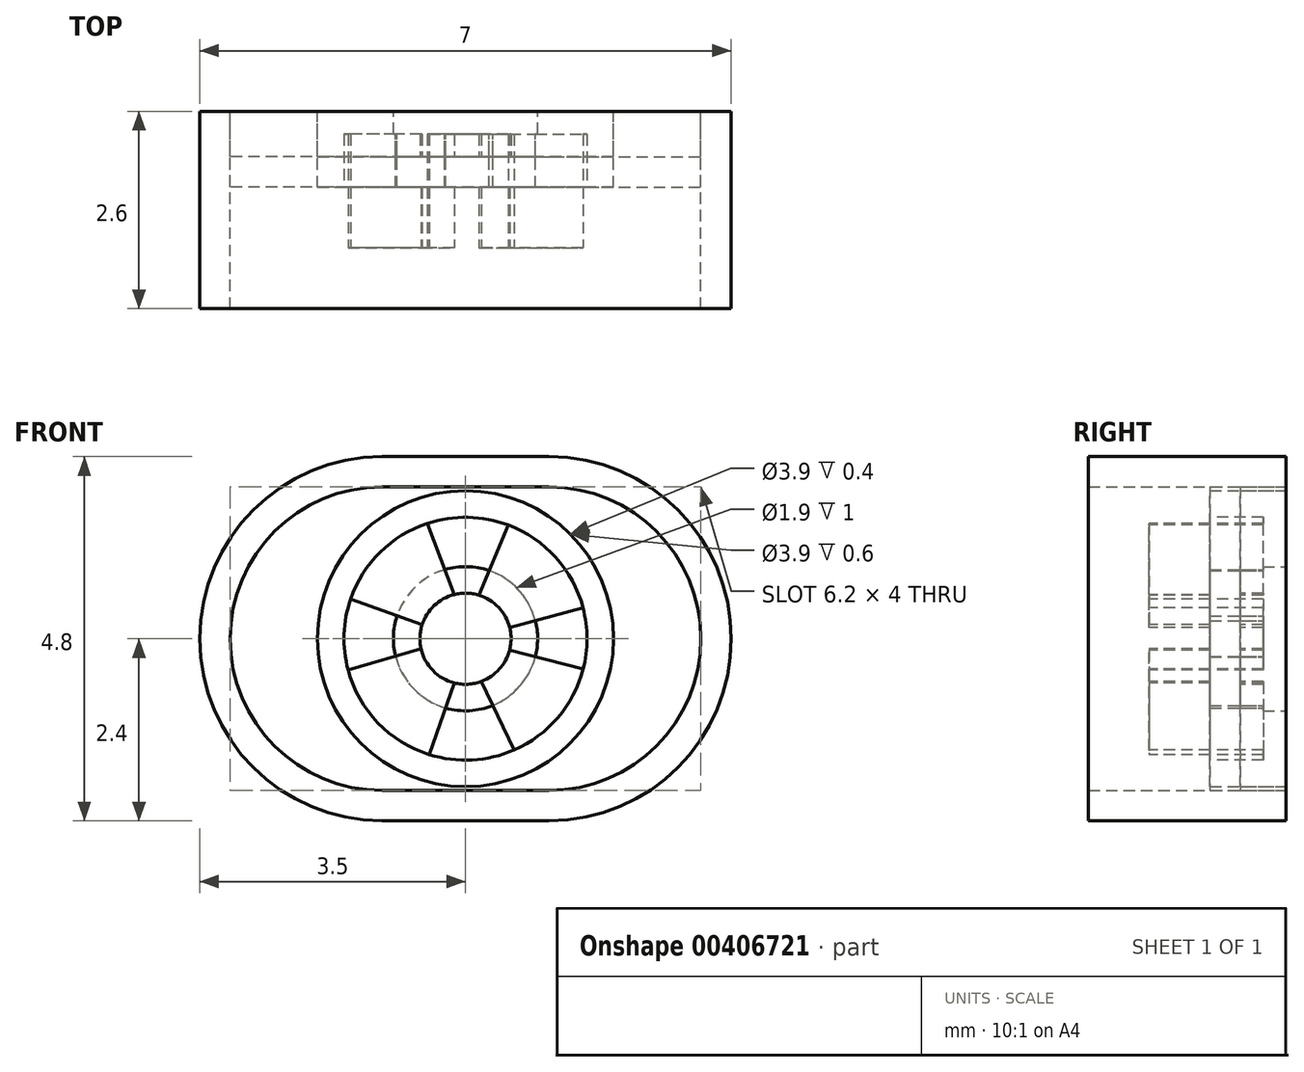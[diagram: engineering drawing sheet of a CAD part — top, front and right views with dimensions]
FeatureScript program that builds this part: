
annotation { "Feature Type Name" : "Feature", "Feature Type Description" : "" }
export const myFeature = defineFeature(function(context is Context, id is Id, definition is map)
    precondition{}
    {
        {
            var Q0;
            Q0=qCreatedBy(makeId("Front.planeOp"),FACE);
            var sketch = newSketch(context, id + "F0", { "sketchPlane" : qUnion([Q0])});
            skLineSegment(sketch, "E0", {"start": v(0, 0) * mm, "end": v(2.2, 0) * mm});
            skLineSegment(sketch, "E1", {"start": v(0, -4.8) * mm, "end": v(2.2, -4.8) * mm});
            skArc(sketch, "E2", {"start": v(0, 0) * mm, "mid": v(-2.4, -2.4) * mm, "end": v(0, -4.8) * mm});
            skArc(sketch, "E3", {"start": v(2.2, -4.8) * mm, "mid": v(4.6, -2.4) * mm, "end": v(2.2, 0) * mm});
            skLineSegment(sketch, "E4.0", {"start": v(0, -4.4) * mm, "end": v(2.2, -4.4) * mm});
            skArc(sketch, "E4.1", {"start": v(0, -0.4) * mm, "mid": v(-2, -2.4) * mm, "end": v(0, -4.4) * mm});
            skLineSegment(sketch, "E4.2", {"start": v(0, -0.4) * mm, "end": v(2.2, -0.4) * mm});
            skArc(sketch, "E4.3", {"start": v(2.2, -4.4) * mm, "mid": v(4.2, -2.4) * mm, "end": v(2.2, -0.4) * mm});
            skCircle(sketch, "E5", {"center": v(1.1, -2.4) * mm, "radius": 0.95 * mm});
            skCircle(sketch, "E6.0", {"center": v(1.1, -2.4) * mm, "radius": 1.95 * mm});
            skSolve(sketch);
        }
        {
            var Q0;
            Q0 = qSketchRegion(id + "F0", true);
            extrude(context, id + "F1", {"entities" : qUnion([Q0]), "depth" : 2.6 * mm});
        }
        {
            var Q0;
            Q0=makeQuery(id+"F0.imprint","IMPRINT",FACE,{"disambiguationData":[TD([[makeQuery(id+"F0.imprint","IMPRINT",EDGE,{"derivedFrom":sQuery(id+"F0.wireOp",EDGE,"E5")}),-1.0]])]});
            extrude(context, id + "F2", {"entities" : qUnion([Q0]), "depth" : 1 * mm});
        }
        {
            var Q0;
            Q0=makeQuery(id+"F0.imprint","IMPRINT",FACE,{"disambiguationData":[TD([[makeQuery(id+"F0.imprint","IMPRINT",EDGE,{"derivedFrom":sQuery(id+"F0.wireOp",EDGE,"E4.0")}),1.0]])]});
            var Q1;
            Q1=makeQuery(id+"F0.imprint","IMPRINT",FACE,{"disambiguationData":[TD([[makeQuery(id+"F0.imprint","IMPRINT",EDGE,{"derivedFrom":sQuery(id+"F0.wireOp",EDGE,"E5")}),1.0]])]});
            extrude(context, id + "F3", {"entities" : qUnion([Q0, Q1]), "depth" : 0.6 * mm});
        }
        {
            var Q0;
            Q0=makeQuery(id+"F2.opExtrude","CAP_FACE",FACE,{"disambiguationData":[OSD([sQuery(id+"F0.wireOp",EDGE,"E5"),sQuery(id+"F0.wireOp",EDGE,"E6.0")])],"isStart":false});
            var sketch = newSketch(context, id + "F4", { "sketchPlane" : qUnion([Q0])});
            skCircle(sketch, "E7", {"center": v(1.1, -2.4) * mm, "radius": 0.6 * mm});
            skCircle(sketch, "E8.0", {"center": v(1.1, -2.4) * mm, "radius": 1.6 * mm});
            skSolve(sketch);
        }
        {
            var Q0;
            Q0=makeQuery(id+"F3.opExtrude","CAP_FACE",FACE,{"disambiguationData":[OSD([sQuery(id+"F0.wireOp",EDGE,"E4.0"),sQuery(id+"F0.wireOp",EDGE,"E4.1"),sQuery(id+"F0.wireOp",EDGE,"E4.2"),sQuery(id+"F0.wireOp",EDGE,"E4.3"),sQuery(id+"F0.wireOp",EDGE,"E6.0")])],"isStart":false});
            extrude(context, id + "F5", {"entities" : qUnion([Q0]), "depth" : 0.4 * mm});
        }
        {
            var Q0;
            Q0=makeQuery(id+"F4.imprint","IMPRINT",FACE,{"disambiguationData":[TD([[makeQuery(id+"F4.imprint","IMPRINT",EDGE,{"derivedFrom":sQuery(id+"F4.wireOp",EDGE,"E7")}),-1.0]])]});
            var Q1;
            Q1=makeQuery(id+"F4.imprint","IMPRINT",FACE,{"disambiguationData":[TD([[makeQuery(id+"F4.imprint","IMPRINT",EDGE,{"derivedFrom":sQuery(id+"F4.wireOp",EDGE,"E8.0")}),1.0]])]});
            extrude(context, id + "F6", {"entities" : qUnion([Q0, Q1]), "operationType" : NewBodyOperationType.ADD, "depth" : 0.8 * mm});
        }
        {
            var Q0;
            Q0=makeQuery(id+"F6.opExtrude","CAP_FACE",FACE,{"disambiguationData":[OSD([sQuery(id+"F4.wireOp",EDGE,"E7"),sQuery(id+"F4.wireOp",EDGE,"E8.0")])],"isStart":false});
            var sketch = newSketch(context, id + "F7", { "sketchPlane" : qUnion([Q0])});
            skLineSegment(sketch, "E9", {"start": v(1.28, -1.83) * mm, "end": v(1.66, -0.9) * mm});
            skLineSegment(sketch, "E10", {"start": v(0.95, -1.82) * mm, "end": v(0.6, -0.88) * mm});
            skLineSegment(sketch, "E11", {"start": v(1.31, -2.96) * mm, "end": v(1.74, -3.87) * mm});
            skLineSegment(sketch, "E12", {"start": v(0.95, -2.98) * mm, "end": v(0.62, -3.93) * mm});
            skLineSegment(sketch, "E13", {"start": v(0.53, -2.22) * mm, "end": v(-0.41, -1.88) * mm});
            skLineSegment(sketch, "E14", {"start": v(0.52, -2.53) * mm, "end": v(-0.45, -2.81) * mm});
            skLineSegment(sketch, "E15", {"start": v(1.68, -2.25) * mm, "end": v(2.65, -2) * mm});
            skLineSegment(sketch, "E16", {"start": v(1.68, -2.55) * mm, "end": v(2.65, -2.8) * mm});
            skSolve(sketch);
        }
        {
            var Q0;
            {var subQ0=sQuery(id+"F7.wireOp",EDGE,"E9");Q0=makeQuery(id+"F7.imprint","IMPRINT",FACE,{"disambiguationData":[TD([[makeQuery(id+"F7.imprint","IMPRINT",EDGE,{"derivedFrom":subQ0}),1.0]])]});}
            var Q1;
            {var subQ0=sQuery(id+"F7.wireOp",EDGE,"E11");Q1=makeQuery(id+"F7.imprint","IMPRINT",FACE,{"disambiguationData":[TD([[makeQuery(id+"F7.imprint","IMPRINT",EDGE,{"derivedFrom":subQ0}),-1.0]])]});}
            extrude(context, id + "F8", {"entities" : qUnion([Q0, Q1]), "operationType" : NewBodyOperationType.REMOVE, "oppositeDirection" : true, "depth" : 1.5 * mm});
        }
        {
            var Q0;
            {var subQ0=sQuery(id+"F7.wireOp",EDGE,"E13");Q0=makeQuery(id+"F7.imprint","IMPRINT",FACE,{"disambiguationData":[TD([[makeQuery(id+"F7.imprint","IMPRINT",EDGE,{"derivedFrom":subQ0}),1.0]])]});}
            var Q1;
            {var subQ0=sQuery(id+"F7.wireOp",EDGE,"E15");Q1=makeQuery(id+"F7.imprint","IMPRINT",FACE,{"disambiguationData":[TD([[makeQuery(id+"F7.imprint","IMPRINT",EDGE,{"derivedFrom":subQ0}),-1.0]])]});}
            extrude(context, id + "F9", {"entities" : qUnion([Q0, Q1]), "operationType" : NewBodyOperationType.REMOVE, "oppositeDirection" : true, "depth" : 1.5 * mm});
        }
    });
